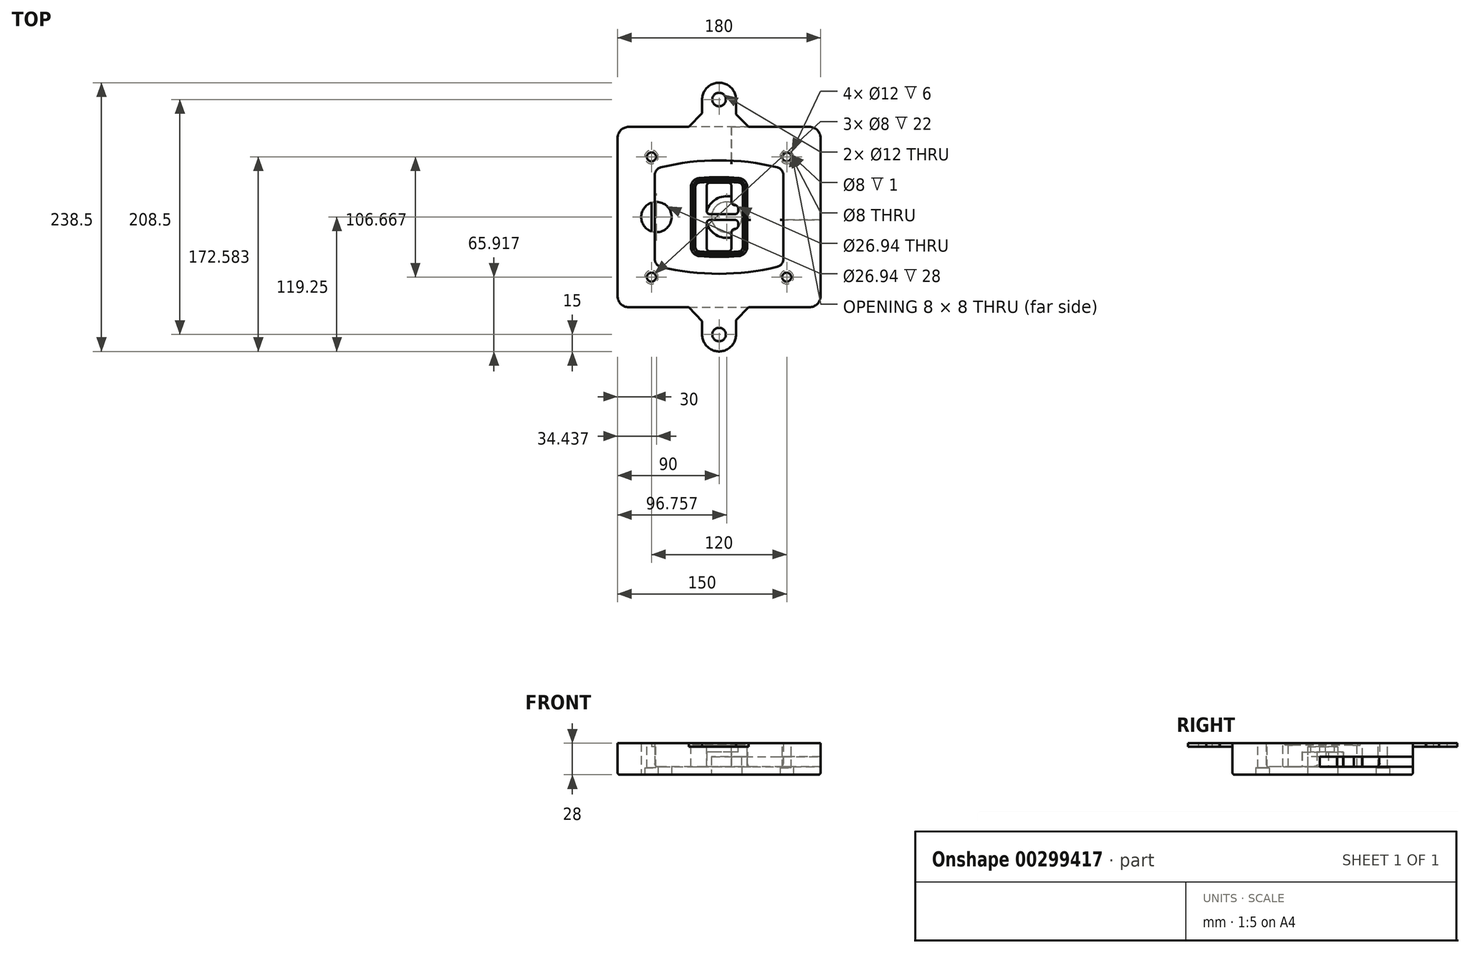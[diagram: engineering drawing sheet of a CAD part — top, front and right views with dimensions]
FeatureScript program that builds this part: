
annotation { "Feature Type Name" : "Feature", "Feature Type Description" : "" }
export const myFeature = defineFeature(function(context is Context, id is Id, definition is map)
    precondition{}
    {
        {
            var Q0;
            Q0=qCreatedBy(makeId("Top.planeOp"),FACE);
            var sketch = newSketch(context, id + "F0", { "sketchPlane" : qUnion([Q0])});
            skPoint(sketch, "E0.rect.middle", {"position": v(0, 0) * mm});
            skLineSegment(sketch, "E1.bottom", {"start": v(-80, -80) * mm, "end": v(80, -80) * mm});
            skLineSegment(sketch, "E1.top", {"start": v(-80, 80) * mm, "end": v(80, 80) * mm});
            skLineSegment(sketch, "E1.left", {"start": v(-90, -70) * mm, "end": v(-90, 70) * mm});
            skLineSegment(sketch, "E1.right", {"start": v(90, -70) * mm, "end": v(90, 70) * mm});
            skLineSegment(sketch, "E2", {"start": v(-90, 80) * mm, "end": v(90, -80) * mm, "construction": true});
            skLineSegment(sketch, "E3", {"start": v(90, 80) * mm, "end": v(-90, -80) * mm, "construction": true});
            skCircle(sketch, "E4", {"center": v(-60, 53.33) * mm, "radius": 4 * mm});
            skCircle(sketch, "E5", {"center": v(60, 53.33) * mm, "radius": 4 * mm});
            skCircle(sketch, "E6", {"center": v(60, -53.33) * mm, "radius": 4 * mm});
            skCircle(sketch, "E7", {"center": v(-60, -53.33) * mm, "radius": 4 * mm});
            skLineSegment(sketch, "E8", {"start": v(-60, 53.33) * mm, "end": v(60, 53.33) * mm, "construction": true});
            skLineSegment(sketch, "E9", {"start": v(60, 53.33) * mm, "end": v(60, -53.33) * mm, "construction": true});
            skLineSegment(sketch, "E10", {"start": v(60, -53.33) * mm, "end": v(-60, -53.33) * mm, "construction": true});
            skLineSegment(sketch, "E11", {"start": v(-60, -53.33) * mm, "end": v(-60, 53.33) * mm, "construction": true});
            skLineSegment(sketch, "E12", {"start": v(-60, 37.3) * mm, "end": v(-60, -37.3) * mm});
            skLineSegment(sketch, "E13", {"start": v(60, 37.3) * mm, "end": v(60, -37.3) * mm});
            skArc(sketch, "E14", {"start": v(52.38, 47.01) * mm, "mid": v(0, 53.33) * mm, "end": v(-52.38, 47.01) * mm});
            skArc(sketch, "E15", {"start": v(-52.38, -47.01) * mm, "mid": v(0, -53.33) * mm, "end": v(52.38, -47.01) * mm});
            skLineSegment(sketch, "E16", {"start": v(-60, 0) * mm, "end": v(60, 0) * mm, "construction": true});
            skPoint(sketch, "E17.visualSharp", {"position": v(-60, -45) * mm});
            skArc(sketch, "E17.filletArc", {"start": v(-60, -37.3) * mm, "mid": v(-57.87, -43.47) * mm, "end": v(-52.38, -47.01) * mm});
            skPoint(sketch, "E18.visualSharp", {"position": v(-60, 45) * mm});
            skArc(sketch, "E18.filletArc", {"start": v(-52.38, 47.01) * mm, "mid": v(-57.87, 43.47) * mm, "end": v(-60, 37.3) * mm});
            skPoint(sketch, "E19.visualSharp", {"position": v(60, 45) * mm});
            skArc(sketch, "E19.filletArc", {"start": v(60, 37.3) * mm, "mid": v(57.87, 43.47) * mm, "end": v(52.38, 47.01) * mm});
            skPoint(sketch, "E20.visualSharp", {"position": v(60, -45) * mm});
            skArc(sketch, "E20.filletArc", {"start": v(52.38, -47.01) * mm, "mid": v(57.87, -43.47) * mm, "end": v(60, -37.3) * mm});
            skPoint(sketch, "E21.visualSharp", {"position": v(-90, 80) * mm});
            skArc(sketch, "E21.filletArc", {"start": v(-80, 80) * mm, "mid": v(-87.07, 77.07) * mm, "end": v(-90, 70) * mm});
            skPoint(sketch, "E22.visualSharp", {"position": v(90, 80) * mm});
            skArc(sketch, "E22.filletArc", {"start": v(90, 70) * mm, "mid": v(87.07, 77.07) * mm, "end": v(80, 80) * mm});
            skPoint(sketch, "E23.visualSharp", {"position": v(90, -80) * mm});
            skArc(sketch, "E23.filletArc", {"start": v(80, -80) * mm, "mid": v(87.07, -77.07) * mm, "end": v(90, -70) * mm});
            skPoint(sketch, "E24.visualSharp", {"position": v(-90, -80) * mm});
            skArc(sketch, "E24.filletArc", {"start": v(-90, -70) * mm, "mid": v(-87.07, -77.07) * mm, "end": v(-80, -80) * mm});
            skArc(sketch, "E25.0", {"start": v(57, 37.3) * mm, "mid": v(55.5, 41.62) * mm, "end": v(51.67, 44.1) * mm});
            skLineSegment(sketch, "E25.1", {"start": v(57, 37.3) * mm, "end": v(57, -37.3) * mm});
            skArc(sketch, "E25.2", {"start": v(51.67, -44.1) * mm, "mid": v(55.5, -41.62) * mm, "end": v(57, -37.3) * mm});
            skArc(sketch, "E25.3", {"start": v(-51.67, -44.1) * mm, "mid": v(0, -50.33) * mm, "end": v(51.67, -44.1) * mm});
            skArc(sketch, "E25.4", {"start": v(-57, -37.3) * mm, "mid": v(-55.5, -41.62) * mm, "end": v(-51.67, -44.1) * mm});
            skArc(sketch, "E25.5", {"start": v(51.67, 44.1) * mm, "mid": v(0, 50.33) * mm, "end": v(-51.67, 44.1) * mm});
            skLineSegment(sketch, "E25.6", {"start": v(-57, 37.3) * mm, "end": v(-57, -37.3) * mm});
            skArc(sketch, "E25.7", {"start": v(-51.67, 44.1) * mm, "mid": v(-55.5, 41.62) * mm, "end": v(-57, 37.3) * mm});
            skArc(sketch, "E26.0", {"start": v(-53.33, 50.9) * mm, "mid": v(-61.01, 45.94) * mm, "end": v(-64, 37.3) * mm});
            skArc(sketch, "E26.1", {"start": v(53.33, 50.9) * mm, "mid": v(0, 57.33) * mm, "end": v(-53.33, 50.9) * mm});
            skArc(sketch, "E26.2", {"start": v(64, 37.3) * mm, "mid": v(61.01, 45.94) * mm, "end": v(53.33, 50.9) * mm});
            skLineSegment(sketch, "E26.3", {"start": v(64, 37.3) * mm, "end": v(64, -37.3) * mm});
            skArc(sketch, "E26.4", {"start": v(53.33, -50.9) * mm, "mid": v(61.01, -45.94) * mm, "end": v(64, -37.3) * mm});
            skLineSegment(sketch, "E26.5", {"start": v(-64, 37.3) * mm, "end": v(-64, -37.3) * mm});
            skArc(sketch, "E26.6", {"start": v(-53.33, -50.9) * mm, "mid": v(0, -57.33) * mm, "end": v(53.33, -50.9) * mm});
            skArc(sketch, "E26.7", {"start": v(-64, -37.3) * mm, "mid": v(-61.01, -45.94) * mm, "end": v(-53.33, -50.9) * mm});
            skSolve(sketch);
        }
        {
            var Q0;
            Q0=makeQuery(id+"F0.imprint","IMPRINT",FACE,{"disambiguationData":[TD([[makeQuery(id+"F0.imprint","IMPRINT",EDGE,{"derivedFrom":sQuery(id+"F0.wireOp",EDGE,"E1.bottom")}),1.0]])]});
            var Q1;
            Q1=makeQuery(id+"F0.imprint","IMPRINT",FACE,{"disambiguationData":[TD([[makeQuery(id+"F0.imprint","IMPRINT",EDGE,{"derivedFrom":sQuery(id+"F0.wireOp",EDGE,"E12")}),1.0]])]});
            var Q2;
            Q2=makeQuery(id+"F0.imprint","IMPRINT",FACE,{"disambiguationData":[TD([[makeQuery(id+"F0.imprint","IMPRINT",EDGE,{"derivedFrom":sQuery(id+"F0.wireOp",EDGE,"E25.0")}),1.0]])]});
            var Q3;
            Q3=makeQuery(id+"F0.imprint","IMPRINT",FACE,{"disambiguationData":[TD([[makeQuery(id+"F0.imprint","IMPRINT",EDGE,{"derivedFrom":sQuery(id+"F0.wireOp",EDGE,"E12")}),-1.0]])]});
            extrude(context, id + "F1", {"entities" : qUnion([Q0, Q1, Q2, Q3]), "oppositeDirection" : true, "depth" : 25 * mm});
        }
        {
            var Q0;
            Q0=makeQuery(id+"F0.imprint","IMPRINT",FACE,{"disambiguationData":[TD([[makeQuery(id+"F0.imprint","IMPRINT",EDGE,{"derivedFrom":sQuery(id+"F0.wireOp",EDGE,"E12")}),1.0]])]});
            extrude(context, id + "F2", {"entities" : qUnion([Q0]), "operationType" : NewBodyOperationType.ADD, "depth" : 3 * mm});
        }
        {
            var Q0;
            Q0=makeQuery(id+"F0.imprint","IMPRINT",FACE,{"disambiguationData":[TD([[makeQuery(id+"F0.imprint","IMPRINT",EDGE,{"derivedFrom":sQuery(id+"F0.wireOp",EDGE,"E25.0")}),1.0]])]});
            extrude(context, id + "F3", {"entities" : qUnion([Q0]), "operationType" : NewBodyOperationType.REMOVE, "oppositeDirection" : true, "depth" : 18 * mm});
        }
        {
            var Q0;
            Q0=makeQuery(id+"F2.opExtrude","CAP_FACE",FACE,{"disambiguationData":[OSD([sQuery(id+"F0.wireOp",EDGE,"E12"),sQuery(id+"F0.wireOp",EDGE,"E13"),sQuery(id+"F0.wireOp",EDGE,"E14"),sQuery(id+"F0.wireOp",EDGE,"E15"),sQuery(id+"F0.wireOp",EDGE,"E17.filletArc"),sQuery(id+"F0.wireOp",EDGE,"E18.filletArc"),sQuery(id+"F0.wireOp",EDGE,"E19.filletArc"),sQuery(id+"F0.wireOp",EDGE,"E20.filletArc"),sQuery(id+"F0.wireOp",EDGE,"E25.0"),sQuery(id+"F0.wireOp",EDGE,"E25.1"),sQuery(id+"F0.wireOp",EDGE,"E25.2"),sQuery(id+"F0.wireOp",EDGE,"E25.3"),sQuery(id+"F0.wireOp",EDGE,"E25.4"),sQuery(id+"F0.wireOp",EDGE,"E25.5"),sQuery(id+"F0.wireOp",EDGE,"E25.6"),sQuery(id+"F0.wireOp",EDGE,"E25.7")])],"isStart":false});
            var sketch = newSketch(context, id + "F4", { "sketchPlane" : qUnion([Q0])});
            skArc(sketch, "E27.0", {"start": v(-17.7, -34.56) * mm, "mid": v(0, -35.33) * mm, "end": v(17.7, -34.56) * mm});
            skArc(sketch, "E28.0", {"start": v(17.7, 34.56) * mm, "mid": v(0, 35.33) * mm, "end": v(-17.7, 34.56) * mm});
            skLineSegment(sketch, "E29", {"start": v(-25, 26.59) * mm, "end": v(-25, -26.59) * mm});
            skLineSegment(sketch, "E30", {"start": v(25, 26.59) * mm, "end": v(25, -26.59) * mm});
            skLineSegment(sketch, "E31", {"start": v(-25, 33.78) * mm, "end": v(25, 33.78) * mm, "construction": true});
            skLineSegment(sketch, "E32", {"start": v(-25, -33.78) * mm, "end": v(25, -33.78) * mm, "construction": true});
            skPoint(sketch, "E33.visualSharp", {"position": v(-25, 33.78) * mm});
            skArc(sketch, "E33.filletArc", {"start": v(-17.7, 34.56) * mm, "mid": v(-22.9, 32) * mm, "end": v(-25, 26.59) * mm});
            skPoint(sketch, "E34.visualSharp", {"position": v(25, 33.78) * mm});
            skArc(sketch, "E34.filletArc", {"start": v(25, 26.59) * mm, "mid": v(22.9, 32) * mm, "end": v(17.7, 34.56) * mm});
            skPoint(sketch, "E35.visualSharp", {"position": v(25, -33.78) * mm});
            skArc(sketch, "E35.filletArc", {"start": v(17.7, -34.56) * mm, "mid": v(22.9, -32) * mm, "end": v(25, -26.59) * mm});
            skPoint(sketch, "E36.visualSharp", {"position": v(-25, -33.78) * mm});
            skArc(sketch, "E36.filletArc", {"start": v(-25, -26.59) * mm, "mid": v(-22.9, -32) * mm, "end": v(-17.7, -34.56) * mm});
            skArc(sketch, "E37.0", {"start": v(51.67, 44.1) * mm, "mid": v(0, 50.33) * mm, "end": v(-51.67, 44.1) * mm});
            skArc(sketch, "E37.1", {"start": v(-51.67, 44.1) * mm, "mid": v(-55.5, 41.62) * mm, "end": v(-57, 37.3) * mm});
            skLineSegment(sketch, "E37.2", {"start": v(-57, 37.3) * mm, "end": v(-57, -37.3) * mm});
            skArc(sketch, "E37.3", {"start": v(-57, -37.3) * mm, "mid": v(-55.5, -41.62) * mm, "end": v(-51.67, -44.1) * mm});
            skArc(sketch, "E37.4", {"start": v(-51.67, -44.1) * mm, "mid": v(0, -50.33) * mm, "end": v(51.67, -44.1) * mm});
            skArc(sketch, "E37.5", {"start": v(51.67, -44.1) * mm, "mid": v(55.5, -41.62) * mm, "end": v(57, -37.3) * mm});
            skLineSegment(sketch, "E37.6", {"start": v(57, 37.3) * mm, "end": v(57, -37.3) * mm});
            skArc(sketch, "E37.7", {"start": v(57, 37.3) * mm, "mid": v(55.5, 41.62) * mm, "end": v(51.67, 44.1) * mm});
            skLineSegment(sketch, "E38.0", {"start": v(23, 26.59) * mm, "end": v(23, -26.59) * mm});
            skArc(sketch, "E38.1", {"start": v(17.53, -32.56) * mm, "mid": v(21.42, -30.64) * mm, "end": v(23, -26.59) * mm});
            skArc(sketch, "E38.2", {"start": v(-17.53, -32.56) * mm, "mid": v(0, -33.33) * mm, "end": v(17.53, -32.56) * mm});
            skArc(sketch, "E38.3", {"start": v(-23, -26.59) * mm, "mid": v(-21.42, -30.64) * mm, "end": v(-17.53, -32.56) * mm});
            skLineSegment(sketch, "E38.4", {"start": v(-23, 26.59) * mm, "end": v(-23, -26.59) * mm});
            skArc(sketch, "E38.5", {"start": v(23, 26.59) * mm, "mid": v(21.42, 30.64) * mm, "end": v(17.53, 32.56) * mm});
            skArc(sketch, "E38.6", {"start": v(-17.53, 32.56) * mm, "mid": v(-21.42, 30.64) * mm, "end": v(-23, 26.59) * mm});
            skArc(sketch, "E38.7", {"start": v(17.53, 32.56) * mm, "mid": v(0, 33.33) * mm, "end": v(-17.53, 32.56) * mm});
            skArc(sketch, "E39.0", {"start": v(21, 26.59) * mm, "mid": v(19.95, 29.29) * mm, "end": v(17.35, 30.57) * mm});
            skLineSegment(sketch, "E39.1", {"start": v(21, 26.59) * mm, "end": v(21, -26.59) * mm});
            skArc(sketch, "E39.2", {"start": v(17.35, -30.57) * mm, "mid": v(19.95, -29.29) * mm, "end": v(21, -26.59) * mm});
            skArc(sketch, "E39.3", {"start": v(-17.35, -30.57) * mm, "mid": v(0, -31.33) * mm, "end": v(17.35, -30.57) * mm});
            skArc(sketch, "E39.4", {"start": v(-21, -26.59) * mm, "mid": v(-19.95, -29.29) * mm, "end": v(-17.35, -30.57) * mm});
            skArc(sketch, "E39.5", {"start": v(17.35, 30.57) * mm, "mid": v(0, 31.33) * mm, "end": v(-17.35, 30.57) * mm});
            skLineSegment(sketch, "E39.6", {"start": v(-21, 26.59) * mm, "end": v(-21, -26.59) * mm});
            skArc(sketch, "E39.7", {"start": v(-17.35, 30.57) * mm, "mid": v(-19.95, 29.29) * mm, "end": v(-21, 26.59) * mm});
            skLineSegment(sketch, "E40", {"start": v(-25, 0) * mm, "end": v(25, 0) * mm, "construction": true});
            skLineSegment(sketch, "E41", {"start": v(-11, 5.5) * mm, "end": v(-11, 27.5) * mm});
            skLineSegment(sketch, "E42", {"start": v(-8, 30.5) * mm, "end": v(8, 30.5) * mm});
            skLineSegment(sketch, "E43", {"start": v(11, 27.5) * mm, "end": v(11, 13.5) * mm});
            skLineSegment(sketch, "E44", {"start": v(14, 10.5) * mm, "end": v(14, 10.5) * mm});
            skLineSegment(sketch, "E45", {"start": v(17, 7.5) * mm, "end": v(17, 5.5) * mm});
            skLineSegment(sketch, "E46", {"start": v(14, 2.5) * mm, "end": v(-8, 2.5) * mm});
            skPoint(sketch, "E47.visualSharp", {"position": v(-11, 30.5) * mm});
            skArc(sketch, "E47.filletArc", {"start": v(-8, 30.5) * mm, "mid": v(-10.12, 29.62) * mm, "end": v(-11, 27.5) * mm});
            skPoint(sketch, "E48.visualSharp", {"position": v(11, 30.5) * mm});
            skArc(sketch, "E48.filletArc", {"start": v(11, 27.5) * mm, "mid": v(10.12, 29.62) * mm, "end": v(8, 30.5) * mm});
            skPoint(sketch, "E49.visualSharp", {"position": v(11, 10.5) * mm});
            skArc(sketch, "E49.filletArc", {"start": v(11, 13.5) * mm, "mid": v(11.88, 11.38) * mm, "end": v(14, 10.5) * mm});
            skPoint(sketch, "E50.visualSharp", {"position": v(17, 10.5) * mm});
            skArc(sketch, "E50.filletArc", {"start": v(17, 7.5) * mm, "mid": v(16.12, 9.62) * mm, "end": v(14, 10.5) * mm});
            skPoint(sketch, "E51.visualSharp", {"position": v(17, 2.5) * mm});
            skArc(sketch, "E51.filletArc", {"start": v(14, 2.5) * mm, "mid": v(16.12, 3.38) * mm, "end": v(17, 5.5) * mm});
            skPoint(sketch, "E52.visualSharp", {"position": v(-11, 2.5) * mm});
            skArc(sketch, "E52.filletArc", {"start": v(-11, 5.5) * mm, "mid": v(-10.12, 3.38) * mm, "end": v(-8, 2.5) * mm});
            skLineSegment(sketch, "E53.0.MirrorCS", {"start": v(14, -2.5) * mm, "end": v(-8, -2.5) * mm});
            skArc(sketch, "E54.0.MirrorCS", {"start": v(-11, -5.5) * mm, "mid": v(-10.12, -3.38) * mm, "end": v(-8, -2.5) * mm});
            skLineSegment(sketch, "E55.0.MirrorCS", {"start": v(-11, -5.5) * mm, "end": v(-11, -27.5) * mm});
            skArc(sketch, "E56.0.MirrorCS", {"start": v(-8, -30.5) * mm, "mid": v(-10.12, -29.62) * mm, "end": v(-11, -27.5) * mm});
            skLineSegment(sketch, "E57.0.MirrorCS", {"start": v(-8, -30.5) * mm, "end": v(8, -30.5) * mm});
            skArc(sketch, "E58.0.MirrorCS", {"start": v(11, -27.5) * mm, "mid": v(10.12, -29.62) * mm, "end": v(8, -30.5) * mm});
            skLineSegment(sketch, "E59.0.MirrorCS", {"start": v(11, -27.5) * mm, "end": v(11, -13.5) * mm});
            skArc(sketch, "E60.0.MirrorCS", {"start": v(11, -13.5) * mm, "mid": v(11.88, -11.38) * mm, "end": v(14, -10.5) * mm});
            skArc(sketch, "E61.0.MirrorCS", {"start": v(17, -7.5) * mm, "mid": v(16.12, -9.62) * mm, "end": v(14, -10.5) * mm});
            skLineSegment(sketch, "E62.0.MirrorCS", {"start": v(17, -7.5) * mm, "end": v(17, -5.5) * mm});
            skArc(sketch, "E63.0.MirrorCS", {"start": v(14, -2.5) * mm, "mid": v(16.12, -3.38) * mm, "end": v(17, -5.5) * mm});
            skSolve(sketch);
        }
        {
            var Q0;
            Q0=makeQuery(id+"F4.imprint","IMPRINT",FACE,{"disambiguationData":[TD([[makeQuery(id+"F4.imprint","IMPRINT",EDGE,{"derivedFrom":sQuery(id+"F4.wireOp",EDGE,"E27.0")}),1.0]])]});
            var Q1;
            Q1=makeQuery(id+"F4.imprint","IMPRINT",FACE,{"disambiguationData":[TD([[makeQuery(id+"F4.imprint","IMPRINT",EDGE,{"derivedFrom":sQuery(id+"F4.wireOp",EDGE,"E38.0")}),-1.0]])]});
            var Q2;
            Q2=makeQuery(id+"F4.imprint","IMPRINT",FACE,{"disambiguationData":[TD([[makeQuery(id+"F4.imprint","IMPRINT",EDGE,{"derivedFrom":sQuery(id+"F4.wireOp",EDGE,"E39.0")}),1.0]])]});
            extrude(context, id + "F5", {"entities" : qUnion([Q0, Q1, Q2]), "operationType" : NewBodyOperationType.ADD, "endBound" : BoundingType.UP_TO_NEXT, "oppositeDirection" : true, "depth" : 25 * mm});
        }
        {
            var Q0;
            Q0=makeQuery(id+"F4.imprint","IMPRINT",FACE,{"disambiguationData":[TD([[makeQuery(id+"F4.imprint","IMPRINT",EDGE,{"derivedFrom":sQuery(id+"F4.wireOp",EDGE,"E38.0")}),-1.0]])]});
            extrude(context, id + "F6", {"entities" : qUnion([Q0]), "operationType" : NewBodyOperationType.REMOVE, "oppositeDirection" : true, "depth" : 2 * mm});
        }
        {
            var Q0;
            Q0=makeQuery(id+"F1.opExtrude","CAP_FACE",FACE,{"disambiguationData":[OSD([sQuery(id+"F0.wireOp",EDGE,"E1.bottom"),sQuery(id+"F0.wireOp",EDGE,"E1.top"),sQuery(id+"F0.wireOp",EDGE,"E1.left"),sQuery(id+"F0.wireOp",EDGE,"E1.right"),sQuery(id+"F0.wireOp",EDGE,"E4"),sQuery(id+"F0.wireOp",EDGE,"E5"),sQuery(id+"F0.wireOp",EDGE,"E6"),sQuery(id+"F0.wireOp",EDGE,"E7"),sQuery(id+"F0.wireOp",EDGE,"E21.filletArc"),sQuery(id+"F0.wireOp",EDGE,"E22.filletArc"),sQuery(id+"F0.wireOp",EDGE,"E23.filletArc"),sQuery(id+"F0.wireOp",EDGE,"E24.filletArc")])],"isStart":false});
            var sketch = newSketch(context, id + "F7", { "sketchPlane" : qUnion([Q0])});
            skCircle(sketch, "E64", {"center": v(6.76, 0) * mm, "radius": 13.47 * mm});
            skCircle(sketch, "E65", {"center": v(-55.56, 0) * mm, "radius": 13.47 * mm});
            skLineSegment(sketch, "E66", {"start": v(90, 0) * mm, "end": v(-90, 0) * mm});
            skCircle(sketch, "E67", {"center": v(6.76, 0) * mm, "radius": 18.47 * mm});
            skCircle(sketch, "E68", {"center": v(60, -53.33) * mm, "radius": 6 * mm});
            skCircle(sketch, "E69", {"center": v(-60, -53.33) * mm, "radius": 6 * mm});
            skCircle(sketch, "E70", {"center": v(-60, 53.33) * mm, "radius": 6 * mm});
            skCircle(sketch, "E71", {"center": v(60, 53.33) * mm, "radius": 6 * mm});
            skSolve(sketch);
        }
        {
            var Q0;
            {var subQ1=sQuery(id+"F7.wireOp",EDGE,"E66");var subQ4=sQuery(id+"F7.wireOp",EDGE,"E64");var subQ6=makeQuery(id+"F7.imprint","INTERSECT",VERTEX,{"disambiguationData":[OD(0.0)],"derivedFrom":[subQ4,subQ1]});Q0=makeQuery(id+"F7.imprint","IMPRINT",FACE,{"disambiguationData":[TD([[makeQuery(id+"F7.imprint","IMPRINT",EDGE,{"disambiguationData":[TD([[subQ6,-1.0]])],"derivedFrom":subQ4}),-1.0]])]});}
            var Q1;
            {var subQ0=sQuery(id+"F7.wireOp",EDGE,"E66");var subQ1=sQuery(id+"F7.wireOp",EDGE,"E64");var subQ3=makeQuery(id+"F7.imprint","INTERSECT",VERTEX,{"disambiguationData":[OD(0.0)],"derivedFrom":[subQ1,subQ0]});Q1=makeQuery(id+"F7.imprint","IMPRINT",FACE,{"disambiguationData":[TD([[makeQuery(id+"F7.imprint","IMPRINT",EDGE,{"disambiguationData":[TD([[subQ3,-1.0]])],"derivedFrom":subQ1}),1.0]])]});}
            var Q2;
            {var subQ0=sQuery(id+"F7.wireOp",EDGE,"E66");var subQ1=sQuery(id+"F7.wireOp",EDGE,"E64");var subQ3=makeQuery(id+"F7.imprint","INTERSECT",VERTEX,{"disambiguationData":[OD(0.0)],"derivedFrom":[subQ1,subQ0]});Q2=makeQuery(id+"F7.imprint","IMPRINT",FACE,{"disambiguationData":[TD([[makeQuery(id+"F7.imprint","IMPRINT",EDGE,{"disambiguationData":[TD([[subQ3,1.0]])],"derivedFrom":subQ1}),1.0]])]});}
            var Q3;
            {var subQ1=sQuery(id+"F7.wireOp",EDGE,"E66");var subQ4=sQuery(id+"F7.wireOp",EDGE,"E64");var subQ6=makeQuery(id+"F7.imprint","INTERSECT",VERTEX,{"disambiguationData":[OD(0.0)],"derivedFrom":[subQ4,subQ1]});Q3=makeQuery(id+"F7.imprint","IMPRINT",FACE,{"disambiguationData":[TD([[makeQuery(id+"F7.imprint","IMPRINT",EDGE,{"disambiguationData":[TD([[subQ6,1.0]])],"derivedFrom":subQ4}),-1.0]])]});}
            extrude(context, id + "F8", {"entities" : qUnion([Q0, Q1, Q2, Q3]), "operationType" : NewBodyOperationType.ADD, "oppositeDirection" : true, "depth" : 20 * mm});
        }
        {
            var Q0;
            {var subQ0=sQuery(id+"F7.wireOp",EDGE,"E66");var subQ1=sQuery(id+"F7.wireOp",EDGE,"E64");var subQ3=makeQuery(id+"F7.imprint","INTERSECT",VERTEX,{"disambiguationData":[OD(0.0)],"derivedFrom":[subQ1,subQ0]});Q0=makeQuery(id+"F7.imprint","IMPRINT",FACE,{"disambiguationData":[TD([[makeQuery(id+"F7.imprint","IMPRINT",EDGE,{"disambiguationData":[TD([[subQ3,-1.0]])],"derivedFrom":subQ1}),1.0]])]});}
            var Q1;
            {var subQ0=sQuery(id+"F7.wireOp",EDGE,"E66");var subQ1=sQuery(id+"F7.wireOp",EDGE,"E64");var subQ3=makeQuery(id+"F7.imprint","INTERSECT",VERTEX,{"disambiguationData":[OD(0.0)],"derivedFrom":[subQ1,subQ0]});Q1=makeQuery(id+"F7.imprint","IMPRINT",FACE,{"disambiguationData":[TD([[makeQuery(id+"F7.imprint","IMPRINT",EDGE,{"disambiguationData":[TD([[subQ3,1.0]])],"derivedFrom":subQ1}),1.0]])]});}
            extrude(context, id + "F9", {"entities" : qUnion([Q0, Q1]), "operationType" : NewBodyOperationType.REMOVE, "oppositeDirection" : true, "depth" : 16 * mm});
        }
        {
            var Q0;
            {var subQ0=sQuery(id+"F7.wireOp",EDGE,"E66");var subQ1=sQuery(id+"F7.wireOp",EDGE,"E65");var subQ3=makeQuery(id+"F7.imprint","INTERSECT",VERTEX,{"disambiguationData":[OD(0.0)],"derivedFrom":[subQ1,subQ0]});Q0=makeQuery(id+"F7.imprint","IMPRINT",FACE,{"disambiguationData":[TD([[makeQuery(id+"F7.imprint","IMPRINT",EDGE,{"disambiguationData":[TD([[subQ3,-1.0]])],"derivedFrom":subQ1}),1.0]])]});}
            var Q1;
            {var subQ0=sQuery(id+"F7.wireOp",EDGE,"E66");var subQ1=sQuery(id+"F7.wireOp",EDGE,"E65");var subQ3=makeQuery(id+"F7.imprint","INTERSECT",VERTEX,{"disambiguationData":[OD(0.0)],"derivedFrom":[subQ1,subQ0]});Q1=makeQuery(id+"F7.imprint","IMPRINT",FACE,{"disambiguationData":[TD([[makeQuery(id+"F7.imprint","IMPRINT",EDGE,{"disambiguationData":[TD([[subQ3,1.0]])],"derivedFrom":subQ1}),1.0]])]});}
            extrude(context, id + "F10", {"entities" : qUnion([Q0, Q1]), "operationType" : NewBodyOperationType.REMOVE, "oppositeDirection" : true, "depth" : 25 * mm});
        }
        {
            var Q0;
            Q0=makeQuery(id+"F7.imprint","IMPRINT",FACE,{"disambiguationData":[TD([[makeQuery(id+"F7.imprint","IMPRINT",EDGE,{"derivedFrom":sQuery(id+"F7.wireOp",EDGE,"E68")}),1.0]])]});
            var Q1;
            Q1=makeQuery(id+"F7.imprint","IMPRINT",FACE,{"disambiguationData":[TD([[makeQuery(id+"F7.imprint","IMPRINT",EDGE,{"derivedFrom":makeQuery(id+"F1.opExtrude","CAP_EDGE",EDGE,{"disambiguationData":[OSD([sQuery(id+"F0.wireOp",EDGE,"E5")])],"isStart":false})}),-1.0]])]});
            var Q2;
            Q2=makeQuery(id+"F7.imprint","IMPRINT",FACE,{"disambiguationData":[TD([[makeQuery(id+"F7.imprint","IMPRINT",EDGE,{"derivedFrom":sQuery(id+"F7.wireOp",EDGE,"E69")}),1.0]])]});
            var Q3;
            Q3=makeQuery(id+"F7.imprint","IMPRINT",FACE,{"disambiguationData":[TD([[makeQuery(id+"F7.imprint","IMPRINT",EDGE,{"derivedFrom":makeQuery(id+"F1.opExtrude","CAP_EDGE",EDGE,{"disambiguationData":[OSD([sQuery(id+"F0.wireOp",EDGE,"E4")])],"isStart":false})}),-1.0]])]});
            var Q4;
            Q4=makeQuery(id+"F7.imprint","IMPRINT",FACE,{"disambiguationData":[TD([[makeQuery(id+"F7.imprint","IMPRINT",EDGE,{"derivedFrom":sQuery(id+"F7.wireOp",EDGE,"E70")}),1.0]])]});
            var Q5;
            Q5=makeQuery(id+"F7.imprint","IMPRINT",FACE,{"disambiguationData":[TD([[makeQuery(id+"F7.imprint","IMPRINT",EDGE,{"derivedFrom":makeQuery(id+"F1.opExtrude","CAP_EDGE",EDGE,{"disambiguationData":[OSD([sQuery(id+"F0.wireOp",EDGE,"E7")])],"isStart":false})}),-1.0]])]});
            var Q6;
            Q6=makeQuery(id+"F7.imprint","IMPRINT",FACE,{"disambiguationData":[TD([[makeQuery(id+"F7.imprint","IMPRINT",EDGE,{"derivedFrom":sQuery(id+"F7.wireOp",EDGE,"E71")}),1.0]])]});
            var Q7;
            Q7=makeQuery(id+"F7.imprint","IMPRINT",FACE,{"disambiguationData":[TD([[makeQuery(id+"F7.imprint","IMPRINT",EDGE,{"derivedFrom":makeQuery(id+"F1.opExtrude","CAP_EDGE",EDGE,{"disambiguationData":[OSD([sQuery(id+"F0.wireOp",EDGE,"E6")])],"isStart":false})}),-1.0]])]});
            extrude(context, id + "F11", {"entities" : qUnion([Q0, Q1, Q2, Q3, Q4, Q5, Q6, Q7]), "operationType" : NewBodyOperationType.REMOVE, "oppositeDirection" : true, "depth" : 6 * mm});
        }
        {
            var Q0;
            Q0=makeQuery(id+"F9.boolean.opBoolean","COPY",FACE,{"derivedFrom":makeQuery(id+"F9.opExtrude","CAP_FACE",FACE,{"disambiguationData":[OSD([sQuery(id+"F7.wireOp",EDGE,"E64")])],"isStart":false})});
            var sketch = newSketch(context, id + "F12", { "sketchPlane" : qUnion([Q0])});
            skArc(sketch, "E72.0", {"start": v(11, -88.19) * mm, "mid": v(97.1, -83.6) * mm, "end": v(92.5, 2.5) * mm});
            skLineSegment(sketch, "E72.1", {"start": v(11, -17.97) * mm, "end": v(11, -17.97) * mm});
            skLineSegment(sketch, "E73", {"start": v(92.5, -105.13) * mm, "end": v(102.3, -105.13) * mm});
            skLineSegment(sketch, "E74.0", {"start": v(92.5, 2.5) * mm, "end": v(14, 2.5) * mm});
            skArc(sketch, "E74.1", {"start": v(14, 2.5) * mm, "mid": v(16.12, 3.38) * mm, "end": v(17, 5.5) * mm});
            skLineSegment(sketch, "E74.2", {"start": v(17, 7.5) * mm, "end": v(17, 5.5) * mm});
            skArc(sketch, "E74.3", {"start": v(17, 7.5) * mm, "mid": v(16.12, 9.62) * mm, "end": v(14, 10.5) * mm});
            skArc(sketch, "E74.4", {"start": v(11, 13.5) * mm, "mid": v(11.88, 11.38) * mm, "end": v(14, 10.5) * mm});
            skLineSegment(sketch, "E74.5", {"start": v(11, 13.5) * mm, "end": v(11, -88.19) * mm});
            skLineSegment(sketch, "E74.7", {"start": v(92.5, -2.5) * mm, "end": v(14, -2.5) * mm});
            skArc(sketch, "E74.8", {"start": v(14, -2.5) * mm, "mid": v(16.12, -3.38) * mm, "end": v(17, -5.5) * mm});
            skLineSegment(sketch, "E74.9", {"start": v(17, -7.5) * mm, "end": v(17, -5.5) * mm});
            skArc(sketch, "E74.10", {"start": v(17, -7.5) * mm, "mid": v(16.12, -9.62) * mm, "end": v(14, -10.5) * mm});
            skArc(sketch, "E74.11", {"start": v(11, -13.5) * mm, "mid": v(11.88, -11.38) * mm, "end": v(14, -10.5) * mm});
            skLineSegment(sketch, "E74.12", {"start": v(11, -17.97) * mm, "end": v(11, -13.5) * mm});
            skPoint(sketch, "E75.orphan", {"position": v(11, -27.5) * mm});
            skPoint(sketch, "E76.orphan", {"position": v(-8, -2.5) * mm});
            skPoint(sketch, "E77.orphan", {"position": v(-8, 2.5) * mm});
            skPoint(sketch, "E78.orphan", {"position": v(11, 27.5) * mm});
            skSolve(sketch);
        }
        {
            var Q0;
            {var subQ7=sQuery(id+"F12.wireOp",EDGE,"E72.0");var subQ14=sQuery(id+"F12.wireOp",EDGE,"E72.1");var subQ16=sQuery(id+"F12.wireOp",EDGE,"E74.1");var subQ18=sQuery(id+"F12.wireOp",EDGE,"E74.8");Q0=qUnion([makeQuery(id+"F12.imprint","IMPRINT",FACE,{"disambiguationData":[TD([[makeQuery(id+"F12.imprint","IMPRINT",EDGE,{"derivedFrom":subQ7}),1.0]])]}),makeQuery(id+"F12.imprint","IMPRINT",FACE,{"disambiguationData":[TD([[makeQuery(id+"F12.imprint","IMPRINT",EDGE,{"derivedFrom":subQ14}),1.0]])]}),makeQuery(id+"F12.imprint","IMPRINT",FACE,{"disambiguationData":[TD([[makeQuery(id+"F12.imprint","IMPRINT",EDGE,{"derivedFrom":subQ16}),1.0]])]}),makeQuery(id+"F12.imprint","IMPRINT",FACE,{"disambiguationData":[TD([[makeQuery(id+"F12.imprint","IMPRINT",EDGE,{"derivedFrom":subQ18}),-1.0]])]})]);}
            var Q1;
            Q1=makeQuery(id+"F5.boolean.opBoolean","SPLIT",FACE,{"disambiguationData":[TD([makeQuery(id+"F5.opExtrude","SWEPT_FACE",FACE,{"disambiguationData":[OSD([sQuery(id+"F4.wireOp",EDGE,"E41")])]})])],"derivedFrom":makeQuery(id+"F3.boolean.opBoolean","COPY",FACE,{"derivedFrom":makeQuery(id+"F3.opExtrude","CAP_FACE",FACE,{"disambiguationData":[OSD([sQuery(id+"F0.wireOp",EDGE,"E25.0"),sQuery(id+"F0.wireOp",EDGE,"E25.1"),sQuery(id+"F0.wireOp",EDGE,"E25.2"),sQuery(id+"F0.wireOp",EDGE,"E25.3"),sQuery(id+"F0.wireOp",EDGE,"E25.4"),sQuery(id+"F0.wireOp",EDGE,"E25.5"),sQuery(id+"F0.wireOp",EDGE,"E25.6"),sQuery(id+"F0.wireOp",EDGE,"E25.7")])],"isStart":false})})});
            extrude(context, id + "F13", {"entities" : qUnion([Q0]), "operationType" : NewBodyOperationType.REMOVE, "endBound" : BoundingType.UP_TO_SURFACE, "endBoundEntityFace" : qUnion([Q1]), "depth" : 25 * mm});
        }
        {
            var Q0;
            Q0=makeQuery(id+"F3.boolean.opBoolean","COPY",EDGE,{"derivedFrom":makeQuery(id+"F3.opExtrude","CAP_EDGE",EDGE,{"disambiguationData":[OSD([sQuery(id+"F0.wireOp",EDGE,"E25.6")])],"isStart":false})});
            var Q1;
            Q1=makeQuery(id+"F8.boolean.opBoolean","INTERSECT",EDGE,{"derivedFrom":[makeQuery(id+"F5.opExtrude","SWEPT_FACE",FACE,{"disambiguationData":[OSD([sQuery(id+"F4.wireOp",EDGE,"E30")])]}),makeQuery(id+"F8.opExtrude","CAP_FACE",FACE,{"disambiguationData":[OSD([sQuery(id+"F7.wireOp",EDGE,"E67")])],"isStart":false})]});
            var Q2;
            Q2=makeQuery(id+"F8.boolean.opBoolean","INTERSECT",EDGE,{"disambiguationData":[OD(1.0)],"derivedFrom":[makeQuery(id+"F5.opExtrude","SWEPT_FACE",FACE,{"disambiguationData":[OSD([sQuery(id+"F4.wireOp",EDGE,"E30")])]}),makeQuery(id+"F8.opExtrude","SWEPT_FACE",FACE,{"disambiguationData":[OSD([sQuery(id+"F7.wireOp",EDGE,"E67")])]})]});
            var Q3;
            {var subQ0=makeQuery(id+"F3.boolean.opBoolean","COPY",FACE,{"derivedFrom":makeQuery(id+"F3.opExtrude","CAP_FACE",FACE,{"disambiguationData":[OSD([sQuery(id+"F0.wireOp",EDGE,"E25.0"),sQuery(id+"F0.wireOp",EDGE,"E25.1"),sQuery(id+"F0.wireOp",EDGE,"E25.2"),sQuery(id+"F0.wireOp",EDGE,"E25.3"),sQuery(id+"F0.wireOp",EDGE,"E25.4"),sQuery(id+"F0.wireOp",EDGE,"E25.5"),sQuery(id+"F0.wireOp",EDGE,"E25.6"),sQuery(id+"F0.wireOp",EDGE,"E25.7")])],"isStart":false})});var subQ1=sQuery(id+"F4.wireOp",EDGE,"E30");Q3=makeQuery(id+"F8.boolean.opBoolean","SPLIT",EDGE,{"disambiguationData":[TD([makeQuery(id+"F5.opExtrude","SWEPT_FACE",FACE,{"disambiguationData":[OSD([sQuery(id+"F4.wireOp",EDGE,"E35.filletArc")])]})])],"derivedFrom":makeQuery(id+"F5.opExtrude","TWEAK_EDGE",EDGE,{"derivedFrom":[subQ0,makeQuery(id+"F4.imprint","IMPRINT",EDGE,{"derivedFrom":subQ1})]})});}
            var Q4;
            {var subQ0=sQuery(id+"F0.wireOp",EDGE,"E25.0");var subQ1=sQuery(id+"F0.wireOp",EDGE,"E25.1");var subQ2=sQuery(id+"F0.wireOp",EDGE,"E25.2");var subQ3=sQuery(id+"F0.wireOp",EDGE,"E25.3");var subQ4=sQuery(id+"F0.wireOp",EDGE,"E25.4");var subQ5=sQuery(id+"F0.wireOp",EDGE,"E25.5");var subQ6=sQuery(id+"F0.wireOp",EDGE,"E25.6");var subQ7=sQuery(id+"F0.wireOp",EDGE,"E25.7");Q4=makeQuery(id+"F8.boolean.opBoolean","INTERSECT",EDGE,{"derivedFrom":[makeQuery(id+"F5.boolean.opBoolean","SPLIT",FACE,{"disambiguationData":[TD([makeQuery(id+"F2.opExtrude","SWEPT_FACE",FACE,{"disambiguationData":[OSD([subQ0])]})])],"derivedFrom":makeQuery(id+"F3.boolean.opBoolean","COPY",FACE,{"derivedFrom":makeQuery(id+"F3.opExtrude","CAP_FACE",FACE,{"disambiguationData":[OSD([subQ0,subQ1,subQ2,subQ3,subQ4,subQ5,subQ6,subQ7])],"isStart":false})})}),makeQuery(id+"F8.opExtrude","SWEPT_FACE",FACE,{"disambiguationData":[OSD([sQuery(id+"F7.wireOp",EDGE,"E67")])]})]});}
            var Q5;
            Q5=makeQuery(id+"F8.boolean.opBoolean","INTERSECT",EDGE,{"disambiguationData":[OD(0.0)],"derivedFrom":[makeQuery(id+"F5.opExtrude","SWEPT_FACE",FACE,{"disambiguationData":[OSD([sQuery(id+"F4.wireOp",EDGE,"E30")])]}),makeQuery(id+"F8.opExtrude","SWEPT_FACE",FACE,{"disambiguationData":[OSD([sQuery(id+"F7.wireOp",EDGE,"E67")])]})]});
            fillet(context, id + "F14", {"entities" : qUnion([Q0, Q1, Q2, Q3, Q4, Q5]), "radius" : 3 * mm, "tangentPropagation" : true, "allowEdgeOverflow" : false});
        }
        {
            var Q0;
            Q0=makeQuery(id+"F1.opExtrude","CAP_EDGE",EDGE,{"disambiguationData":[OSD([sQuery(id+"F0.wireOp",EDGE,"E1.bottom")])],"isStart":false});
            fillet(context, id + "F15", {"entities" : qUnion([Q0]), "radius" : 2 * mm, "tangentPropagation" : true, "allowEdgeOverflow" : false});
        }
        {
            var Q0;
            {var subQ0=sQuery(id+"F0.wireOp",EDGE,"E21.filletArc");var subQ1=sQuery(id+"F0.wireOp",EDGE,"E7");var subQ2=sQuery(id+"F0.wireOp",EDGE,"E6");var subQ3=sQuery(id+"F0.wireOp",EDGE,"E5");var subQ4=sQuery(id+"F0.wireOp",EDGE,"E4");var subQ5=sQuery(id+"F0.wireOp",EDGE,"E22.filletArc");var subQ6=sQuery(id+"F0.wireOp",EDGE,"E1.bottom");var subQ7=sQuery(id+"F0.wireOp",EDGE,"E1.right");var subQ8=sQuery(id+"F0.wireOp",EDGE,"E1.top");var subQ9=sQuery(id+"F0.wireOp",EDGE,"E1.left");var subQ10=sQuery(id+"F0.wireOp",EDGE,"E23.filletArc");var subQ11=sQuery(id+"F0.wireOp",EDGE,"E24.filletArc");Q0=makeQuery(id+"F2.boolean.opBoolean","SPLIT",FACE,{"disambiguationData":[TD([makeQuery(id+"F1.opExtrude","SWEPT_FACE",FACE,{"disambiguationData":[OSD([subQ6])]})])],"derivedFrom":makeQuery(id+"F1.opExtrude","CAP_FACE",FACE,{"disambiguationData":[OSD([subQ6,subQ8,subQ9,subQ7,subQ4,subQ3,subQ2,subQ1,subQ0,subQ5,subQ10,subQ11])],"isStart":true})});}
            var sketch = newSketch(context, id + "F16", { "sketchPlane" : qUnion([Q0])});
            skSolve(sketch);
        }
        {
            var Q0;
            Q0=makeQuery(id+"F16.imprint","IMPRINT",FACE,{"disambiguationData":[TD([[makeQuery(id+"F16.imprint","IMPRINT",EDGE,{"derivedFrom":makeQuery(id+"F1.opExtrude","CAP_EDGE",EDGE,{"disambiguationData":[OSD([sQuery(id+"F0.wireOp",EDGE,"E1.bottom")])],"isStart":true})}),1.0]])]});
            var sketch = newSketch(context, id + "F17", { "sketchPlane" : qUnion([Q0])});
            skCircle(sketch, "E79", {"center": v(0, 104.25) * mm, "radius": 6 * mm});
            skLineSegment(sketch, "E80", {"start": v(0, 104.25) * mm, "end": v(0, 74.43) * mm, "construction": true});
            skArc(sketch, "E81", {"start": v(14.97, 103.28) * mm, "mid": v(0.49, 119.24) * mm, "end": v(-15, 104.25) * mm});
            skLineSegment(sketch, "E82", {"start": v(-15, 104.25) * mm, "end": v(-15, 92.25) * mm});
            skLineSegment(sketch, "E83", {"start": v(14.97, 103.28) * mm, "end": v(14.97, 91.28) * mm});
            skLineSegment(sketch, "E84", {"start": v(-15, 92.25) * mm, "end": v(-26.72, 80) * mm});
            skLineSegment(sketch, "E85", {"start": v(14.97, 91.28) * mm, "end": v(26.24, 80) * mm});
            skLineSegment(sketch, "E86", {"start": v(-100.58, 0) * mm, "end": v(124.26, 0) * mm, "construction": true});
            skLineSegment(sketch, "E87.MirrorCS", {"start": v(-15, -92.25) * mm, "end": v(-26.72, -80) * mm});
            skLineSegment(sketch, "E88.MirrorCS", {"start": v(-15, -104.25) * mm, "end": v(-15, -92.25) * mm});
            skArc(sketch, "E89.MirrorCS", {"start": v(14.97, -103.28) * mm, "mid": v(0.49, -119.24) * mm, "end": v(-15, -104.25) * mm});
            skCircle(sketch, "E90.MirrorC", {"center": v(0, -104.25) * mm, "radius": 6 * mm});
            skLineSegment(sketch, "E91.MirrorCS", {"start": v(0, -104.25) * mm, "end": v(0, -74.43) * mm, "construction": true});
            skLineSegment(sketch, "E92.MirrorCS", {"start": v(14.97, -103.28) * mm, "end": v(14.97, -91.28) * mm});
            skLineSegment(sketch, "E93.MirrorCS", {"start": v(14.97, -91.28) * mm, "end": v(26.24, -80) * mm});
            skSolve(sketch);
        }
        {
            var Q0;
            {var subQ0=sQuery(id+"F17.wireOp",EDGE,"E87.MirrorCS");Q0=makeQuery(id+"F17.imprint","IMPRINT",FACE,{"disambiguationData":[TD([[makeQuery(id+"F17.imprint","IMPRINT",EDGE,{"derivedFrom":subQ0}),-1.0]])]});}
            var Q1;
            Q1=makeQuery(id+"F17.imprint","IMPRINT",FACE,{"disambiguationData":[TD([[makeQuery(id+"F17.imprint","IMPRINT",EDGE,{"derivedFrom":sQuery(id+"F17.wireOp",EDGE,"E79")}),-1.0]])]});
            var Q2;
            {var subQ6=sQuery(id+"F0.wireOp",EDGE,"E1.bottom");Q2=makeQuery(id+"F16.imprint","IMPRINT",FACE,{"disambiguationData":[TD([[makeQuery(id+"F16.imprint","IMPRINT",EDGE,{"derivedFrom":makeQuery(id+"F1.opExtrude","CAP_EDGE",EDGE,{"disambiguationData":[OSD([subQ6])],"isStart":true})}),1.0]])]});}
            var Q3;
            Q3=sQuery(id+"F17.wireOp",EDGE,"E84");
            var Q4;
            Q4=sQuery(id+"F17.wireOp",EDGE,"E82");
            var Q5;
            Q5=sQuery(id+"F17.wireOp",EDGE,"E81");
            var Q6;
            Q6=sQuery(id+"F17.wireOp",EDGE,"E79");
            var Q7;
            Q7=sQuery(id+"F17.wireOp",EDGE,"E83");
            var Q8;
            Q8=sQuery(id+"F17.wireOp",EDGE,"E85");
            var Q9;
            Q9=sQuery(id+"F17.wireOp",EDGE,"E93.MirrorCS");
            var Q10;
            Q10=sQuery(id+"F17.wireOp",EDGE,"E87.MirrorCS");
            var Q11;
            Q11=sQuery(id+"F17.wireOp",EDGE,"E88.MirrorCS");
            var Q12;
            Q12=sQuery(id+"F17.wireOp",EDGE,"E89.MirrorCS");
            var Q13;
            Q13=sQuery(id+"F17.wireOp",EDGE,"E90.MirrorC");
            var Q14;
            Q14=sQuery(id+"F17.wireOp",EDGE,"E92.MirrorCS");
            var Q15;
            Q15=makeQuery(id+"F2.opExtrude","CAP_FACE",FACE,{"disambiguationData":[OSD([sQuery(id+"F0.wireOp",EDGE,"E12"),sQuery(id+"F0.wireOp",EDGE,"E13"),sQuery(id+"F0.wireOp",EDGE,"E14"),sQuery(id+"F0.wireOp",EDGE,"E15"),sQuery(id+"F0.wireOp",EDGE,"E17.filletArc"),sQuery(id+"F0.wireOp",EDGE,"E18.filletArc"),sQuery(id+"F0.wireOp",EDGE,"E19.filletArc"),sQuery(id+"F0.wireOp",EDGE,"E20.filletArc"),sQuery(id+"F0.wireOp",EDGE,"E25.0"),sQuery(id+"F0.wireOp",EDGE,"E25.1"),sQuery(id+"F0.wireOp",EDGE,"E25.2"),sQuery(id+"F0.wireOp",EDGE,"E25.3"),sQuery(id+"F0.wireOp",EDGE,"E25.4"),sQuery(id+"F0.wireOp",EDGE,"E25.5"),sQuery(id+"F0.wireOp",EDGE,"E25.6"),sQuery(id+"F0.wireOp",EDGE,"E25.7")])],"isStart":false});
            extrude(context, id + "F18", {"entities" : qUnion([Q0, Q1, Q2]), "operationType" : NewBodyOperationType.ADD, "surfaceEntities" : qUnion([Q3, Q4, Q5, Q6, Q7, Q8, Q9, Q10, Q11, Q12, Q13, Q14]), "endBound" : BoundingType.UP_TO_SURFACE, "endBoundEntityFace" : qUnion([Q15]), "depth" : 25 * mm});
        }
    });
